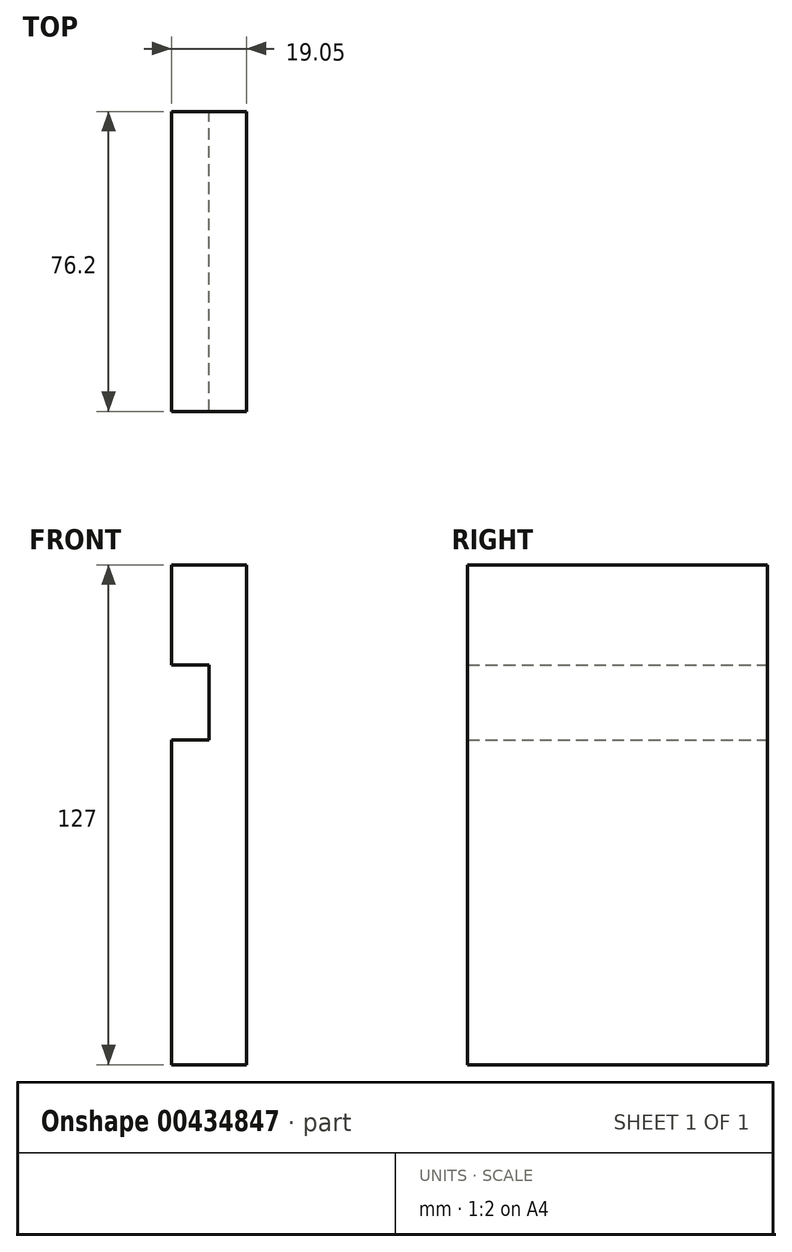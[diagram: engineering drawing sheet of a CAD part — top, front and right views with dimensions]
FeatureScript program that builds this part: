
annotation { "Feature Type Name" : "Feature", "Feature Type Description" : "" }
export const myFeature = defineFeature(function(context is Context, id is Id, definition is map)
    precondition{}
    {
        {
            var Q0;
            Q0=qCreatedBy(makeId("Front.planeOp"),FACE);
            var sketch = newSketch(context, id + "F0", { "sketchPlane" : qUnion([Q0])});
            skLineSegment(sketch, "E0", {"start": v(0, -50.52) * mm, "end": v(0, 76.48) * mm});
            skLineSegment(sketch, "E1", {"start": v(0, -50.52) * mm, "end": v(-19.05, -50.52) * mm});
            skLineSegment(sketch, "E2", {"start": v(-19.05, -50.52) * mm, "end": v(-19.05, 32.03) * mm});
            skLineSegment(sketch, "E3", {"start": v(-19.05, 32.03) * mm, "end": v(-9.53, 32.03) * mm});
            skLineSegment(sketch, "E4", {"start": v(-9.53, 32.03) * mm, "end": v(-9.53, 51.08) * mm});
            skLineSegment(sketch, "E5", {"start": v(-9.53, 51.08) * mm, "end": v(-19.05, 51.08) * mm});
            skLineSegment(sketch, "E6", {"start": v(-19.05, 51.08) * mm, "end": v(-19.05, 76.48) * mm});
            skLineSegment(sketch, "E7", {"start": v(-19.05, 76.48) * mm, "end": v(0, 76.48) * mm});
            skSolve(sketch);
        }
        {
            var Q0;
            Q0 = qSketchRegion(id + "F0", true);
            extrude(context, id + "F1", {"entities" : qUnion([Q0]), "depth" : 76.2 * mm});
        }
    });
